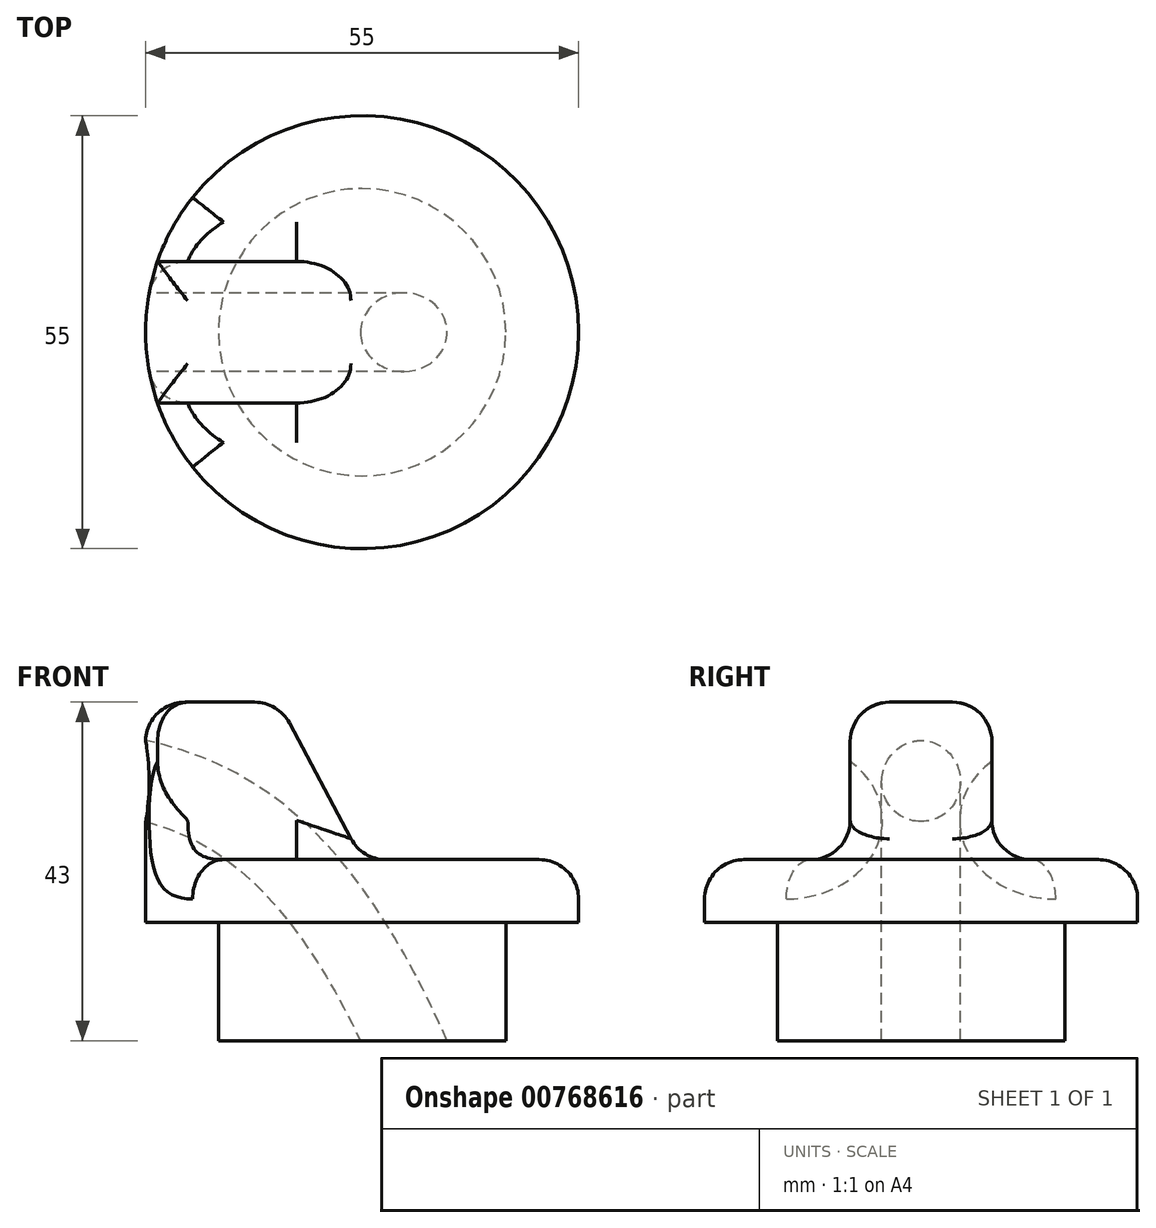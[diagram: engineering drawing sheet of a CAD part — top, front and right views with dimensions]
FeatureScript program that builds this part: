
annotation { "Feature Type Name" : "Feature", "Feature Type Description" : "" }
export const myFeature = defineFeature(function(context is Context, id is Id, definition is map)
    precondition{}
    {
        {
            var Q0;
            Q0=qCreatedBy(makeId("Top.planeOp"),FACE);
            var sketch = newSketch(context, id + "F0", { "sketchPlane" : qUnion([Q0])});
            skCircle(sketch, "E0", {"center": v(0, 0) * mm, "radius": 18.25 * mm});
            skSolve(sketch);
        }
        {
            var Q0;
            Q0=makeQuery(id+"F0.imprint","IMPRINT",FACE,{"disambiguationData":[TD([[makeQuery(id+"F0.imprint","IMPRINT",EDGE,{"derivedFrom":sQuery(id+"F0.wireOp",EDGE,"E0")}),1.0]])]});
            extrude(context, id + "F1", {"entities" : qUnion([Q0]), "depth" : 15 * mm, "offsetDistance" : 25 * mm});
        }
        {
            var Q0;
            Q0=makeQuery(id+"F1.opExtrude","CAP_FACE",FACE,{"disambiguationData":[OSD([sQuery(id+"F0.wireOp",EDGE,"E0")])],"isStart":false});
            var sketch = newSketch(context, id + "F2", { "sketchPlane" : qUnion([Q0])});
            skCircle(sketch, "E1", {"center": v(0, 0) * mm, "radius": 27.5 * mm});
            skSolve(sketch);
        }
        {
            var Q0;
            Q0=makeQuery(id+"F2.imprint","IMPRINT",FACE,{"disambiguationData":[TD([[makeQuery(id+"F2.imprint","IMPRINT",EDGE,{"derivedFrom":sQuery(id+"F2.wireOp",EDGE,"E1")}),1.0]])]});
            var Q1;
            Q1=makeQuery(id+"F2.imprint","IMPRINT",FACE,{"disambiguationData":[TD([[makeQuery(id+"F2.imprint","IMPRINT",EDGE,{"derivedFrom":makeQuery(id+"F1.opExtrude","CAP_EDGE",EDGE,{"disambiguationData":[OSD([sQuery(id+"F0.wireOp",EDGE,"E0")])],"isStart":false})}),1.0]])]});
            extrude(context, id + "F3", {"entities" : qUnion([Q0, Q1]), "operationType" : NewBodyOperationType.ADD, "depth" : 8 * mm, "offsetDistance" : 25 * mm});
        }
        {
            var Q0;
            Q0=qCreatedBy(makeId("Front.planeOp"),FACE);
            var sketch = newSketch(context, id + "F4", { "sketchPlane" : qUnion([Q0])});
            skLineSegment(sketch, "E2.0.0", {"start": v(-27.5, 23) * mm, "end": v(27.5, 23) * mm});
            skLineSegment(sketch, "E3", {"start": v(0, 23) * mm, "end": v(-10.64, 43) * mm});
            skLineSegment(sketch, "E4", {"start": v(-10.64, 43) * mm, "end": v(-27.5, 43) * mm});
            skLineSegment(sketch, "E5", {"start": v(-27.5, 43) * mm, "end": v(-27.5, 23) * mm});
            skFitSpline(sketch, "E6", {"points": [v(-56.7, 35.34) * mm, v(-18.21, 29.5) * mm, v(13.21, -20.32) * mm], "startDerivative": vector(105.11, -3.46) * mm, "endDerivative": vector(49.34, -146.94) * mm});
            skPoint(sketch, "E7", {"position": v(-27.5, 33) * mm});
            skSolve(sketch);
        }
        {
            var Q0;
            Q0=sQuery(id+"F4.wireOp",EDGE,"E6");
            var Q1;
            Q1=sQuery(id+"F4.wireOp",VERTEX,"E6.start");
            cPlane(context, id + "F5", {"entities" : qUnion([Q0, Q1]), "cplaneType" : CPlaneType.CURVE_POINT, "offset" : 25 * mm, "width" : 150 * mm, "height" : 150 * mm});
        }
        {
            var Q0;
            Q0=qCreatedBy(id+"F5.planeOp",FACE);
            var sketch = newSketch(context, id + "F6", { "sketchPlane" : qUnion([Q0])});
            skPoint(sketch, "E8.0", {"position": v(0, 33.45) * mm});
            skCircle(sketch, "E9", {"center": v(0, 33.45) * mm, "radius": 5 * mm});
            skSolve(sketch);
        }
        {
            var Q0;
            {var subQ2=sQuery(id+"F4.wireOp",EDGE,"E3");Q0=makeQuery(id+"F4.imprint","IMPRINT",FACE,{"disambiguationData":[TD([[makeQuery(id+"F4.imprint","IMPRINT",EDGE,{"derivedFrom":subQ2}),1.0]])]});}
            var Q1;
            {var subQ0=sQuery(id+"F4.wireOp",EDGE,"E5");var subQ1=sQuery(id+"F4.wireOp",EDGE,"E2.0.0");var subQ2=makeQuery(id+"F4.imprint","INTERSECT",VERTEX,{"derivedFrom":[subQ1,subQ0]});Q1=makeQuery(id+"F4.imprint","IMPRINT",FACE,{"disambiguationData":[TD([[makeQuery(id+"F4.imprint","IMPRINT",EDGE,{"disambiguationData":[TD([[subQ2,-1.0]])],"derivedFrom":subQ1}),1.0]])]});}
            extrude(context, id + "F7", {"entities" : qUnion([Q0, Q1]), "operationType" : NewBodyOperationType.ADD, "endBound" : BoundingType.SYMMETRIC, "depth" : 18 * mm, "offsetDistance" : 25 * mm});
        }
        {
            var Q0;
            Q0=makeQuery(id+"F6.imprint","IMPRINT",FACE,{"disambiguationData":[TD([[makeQuery(id+"F6.imprint","IMPRINT",EDGE,{"derivedFrom":sQuery(id+"F6.wireOp",EDGE,"E9")}),1.0]])]});
            var Q1;
            Q1=sQuery(id+"F4.wireOp",EDGE,"E6");
            sweep(context, id + "F8", {"operationType" : NewBodyOperationType.REMOVE, "profiles" : qUnion([Q0]), "path" : qUnion([Q1])});
        }
        {
            var Q0;
            {var subQ0=sQuery(id+"F4.wireOp",EDGE,"E5");var subQ1=sQuery(id+"F4.wireOp",EDGE,"E2.0.0");var subQ2=makeQuery(id+"F7.opExtrude","SWEPT_FACE",FACE,{"disambiguationData":[OSD([subQ1])]});Q0=makeQuery(id+"F7.boolean.opBoolean","SPLIT",FACE,{"disambiguationData":[TD([makeQuery(id+"F7.opExtrude","CAP_FACE",FACE,{"disambiguationData":[OSD([subQ1,sQuery(id+"F4.wireOp",EDGE,"E3"),sQuery(id+"F4.wireOp",EDGE,"E4"),subQ0])],"isStart":false})])],"derivedFrom":subQ2});}
            var sketch = newSketch(context, id + "F9", { "sketchPlane" : qUnion([Q0])});
            skLineSegment(sketch, "E10.0.0", {"start": v(-27.5, 9) * mm, "end": v(-27.5, 0) * mm});
            skArc(sketch, "E10.0.1", {"start": v(-27.5, 0) * mm, "mid": v(-27.12, 4.56) * mm, "end": v(-25.99, 9) * mm});
            skLineSegment(sketch, "E10.0.2", {"start": v(-25.99, 9) * mm, "end": v(-27.5, 9) * mm});
            skLineSegment(sketch, "E11.0.0", {"start": v(-27.5, -9) * mm, "end": v(-25.99, -9) * mm});
            skArc(sketch, "E11.0.1", {"start": v(-25.99, -9) * mm, "mid": v(-27.12, -4.56) * mm, "end": v(-27.5, 0) * mm});
            skLineSegment(sketch, "E11.0.2", {"start": v(-27.5, 0) * mm, "end": v(-27.5, -9) * mm});
            skSolve(sketch);
        }
        {
            var Q0;
            Q0=makeQuery(id+"F9.imprint","IMPRINT",FACE,{"disambiguationData":[TD([[makeQuery(id+"F9.imprint","IMPRINT",EDGE,{"derivedFrom":sQuery(id+"F9.wireOp",EDGE,"E11.0.0")}),1.0]])]});
            var Q1;
            Q1=makeQuery(id+"F9.imprint","IMPRINT",FACE,{"disambiguationData":[TD([[makeQuery(id+"F9.imprint","IMPRINT",EDGE,{"derivedFrom":sQuery(id+"F9.wireOp",EDGE,"E10.0.0")}),1.0]])]});
            extrude(context, id + "F10", {"entities" : qUnion([Q0, Q1]), "operationType" : NewBodyOperationType.REMOVE, "endBound" : BoundingType.THROUGH_ALL, "oppositeDirection" : true, "depth" : 25 * mm, "offsetDistance" : 25 * mm});
        }
        {
            var Q0;
            Q0=makeQuery(id+"F3.opExtrude","CAP_FACE",FACE,{"disambiguationData":[OSD([sQuery(id+"F2.wireOp",EDGE,"E1")])],"isStart":false});
            var Q1;
            Q1=makeQuery(id+"F7.opExtrude","SWEPT_FACE",FACE,{"disambiguationData":[OSD([sQuery(id+"F4.wireOp",EDGE,"E4")])]});
            var Q2;
            Q2=makeQuery(id+"F7.opExtrude","SWEPT_FACE",FACE,{"disambiguationData":[OSD([sQuery(id+"F4.wireOp",EDGE,"E3")])]});
            fillet(context, id + "F11", {"entities" : qUnion([Q0, Q1, Q2]), "radius" : 5 * mm, "tangentPropagation" : true, "allowEdgeOverflow" : false});
        }
    });
